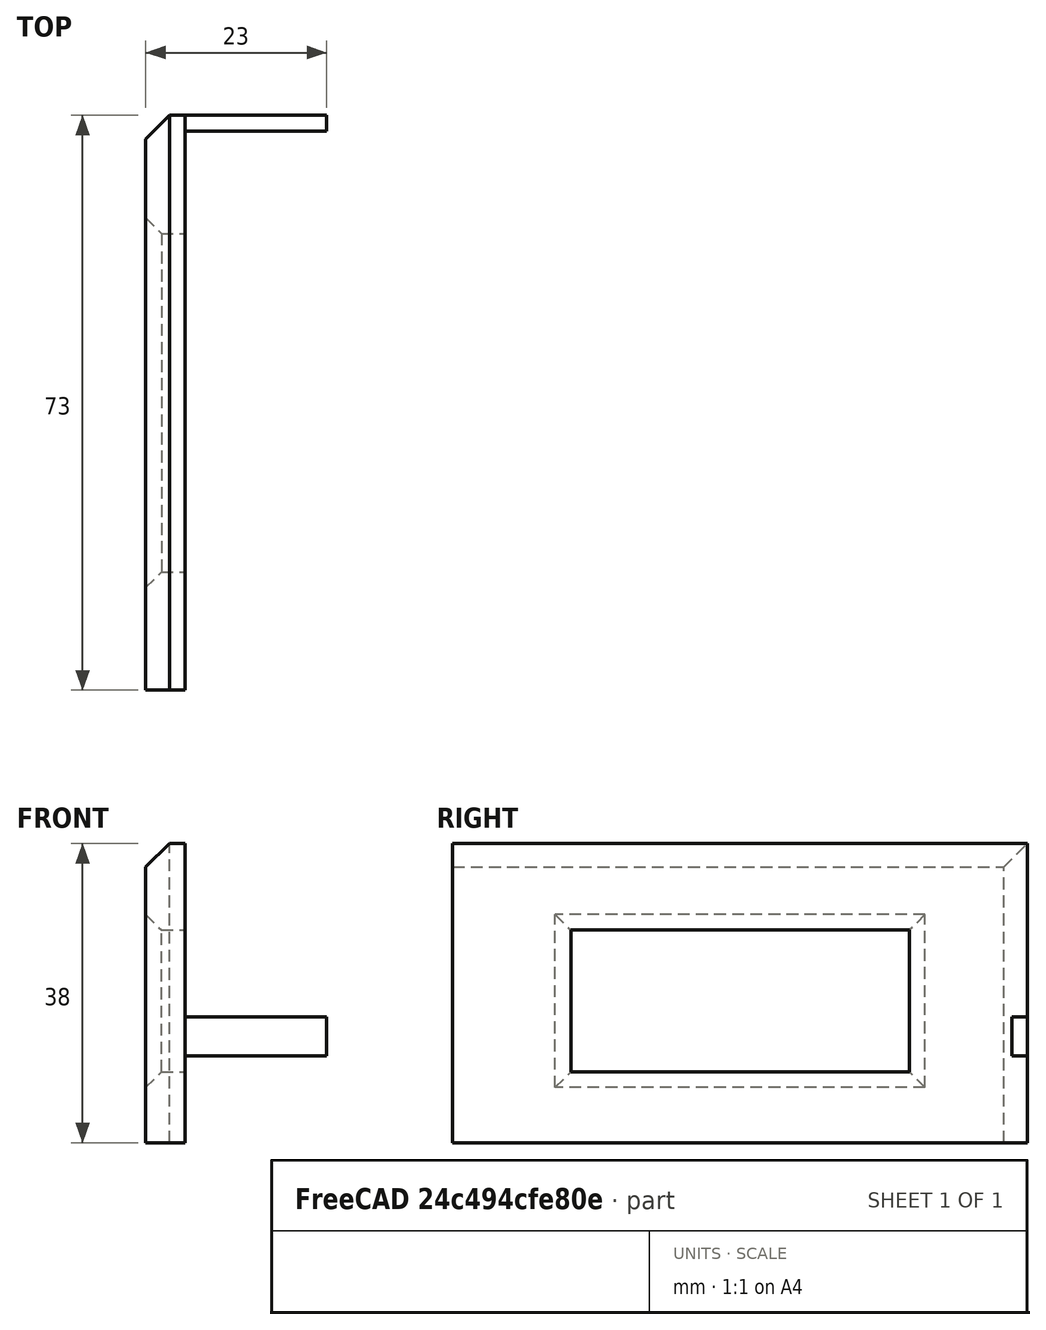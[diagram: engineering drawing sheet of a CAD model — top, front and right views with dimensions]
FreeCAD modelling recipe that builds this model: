
FCSTD DOCUMENT  (FreeCAD 0.21R33694 (Git))
Label: rejillas-lipo
License: Creative Commons Attribution-NonCommercial-ShareAlike 4.0
LicenseURL: https://creativecommons.org/licenses/by-nc-sa/4.0/
objects: Part::Box×3, Part::Chamfer×2, Part::Cut×1, Part::Fuse×1
note: 7 computed .brp shape members not serialized (recipe doc carries the construction recipe); baked Part::Feature solids carry a one-line shape summary decoded from their .brp

FEATURE [Part::Box] Box010  label="restriccion-lipo"
  AttacherType = Attacher::AttachEngine3D
  Height = 38
  Length = 5
  Placement = pos=(17,-75,5) rot=(0,0,1;0rad)
  Width = 73
FEATURE [Part::Box] Box011  label="restriccion-lipo001"
  AttacherType = Attacher::AttachEngine3D
  Height = 18
  Length = 7
  Placement = pos=(16,-60,14) rot=(0,0,1;0rad)
  Width = 43
FEATURE [Part::Box] Box012  label="Cube004"
  AttacherType = Attacher::AttachEngine3D
  Height = 5
  Length = 20
  Placement = pos=(20,-4,16) rot=(0,0,1;0rad)
  Width = 2
FEATURE [Part::Cut] Cut028
  Base = -> Box010
  Refine = true
  Tool = -> Box011
FEATURE [Part::Chamfer] Chamfer002
  Base = -> Cut028
  Edges = 2 edges r=3: [Edge2,Edge4]
FEATURE [Part::Chamfer] Chamfer003
  Base = -> Chamfer002
  Edges = 4 edges r=2: [Edge5,Edge6,Edge7,Edge8]
FEATURE [Part::Fuse] Fusion001032  label="rejillas-lipo"
  Base = -> Chamfer003
  Refine = true
  Tool = -> Box012
